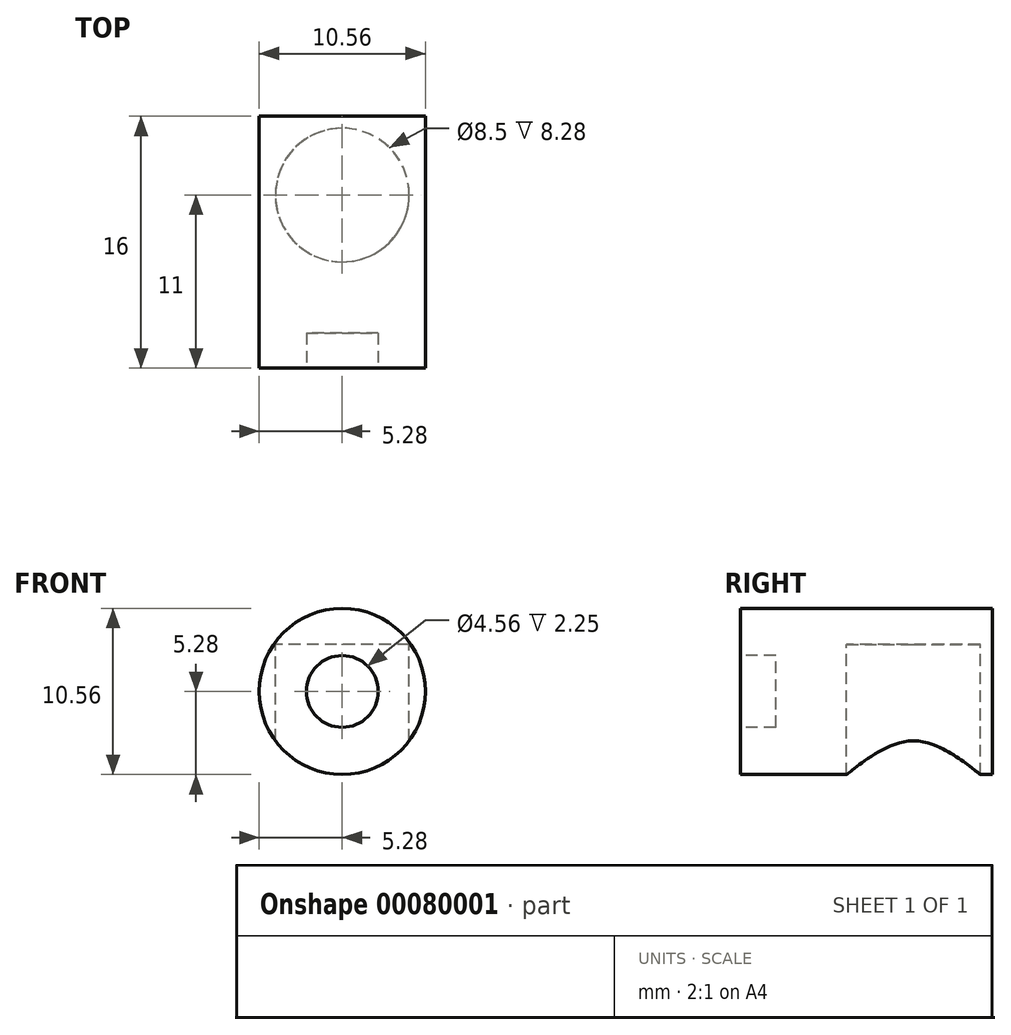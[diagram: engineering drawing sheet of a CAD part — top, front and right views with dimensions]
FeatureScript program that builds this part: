
annotation { "Feature Type Name" : "Feature", "Feature Type Description" : "" }
export const myFeature = defineFeature(function(context is Context, id is Id, definition is map)
    precondition{}
    {
        {
            var Q0;
            Q0=qCreatedBy(makeId("Front.planeOp"),FACE);
            var sketch = newSketch(context, id + "F0", { "sketchPlane" : qUnion([Q0])});
            skCircle(sketch, "E0", {"center": v(0, 0) * mm, "radius": 5.28 * mm});
            skSolve(sketch);
        }
        {
            var Q0;
            Q0 = qSketchRegion(id + "F0", true);
            extrude(context, id + "F1", {"entities" : qUnion([Q0]), "depth" : 16 * mm});
        }
        {
            var Q0;
            Q0=makeQuery(id+"F1.opExtrude","CAP_FACE",FACE,{"disambiguationData":[OSD([sQuery(id+"F0.wireOp",EDGE,"E0")])],"isStart":false});
            var sketch = newSketch(context, id + "F2", { "sketchPlane" : qUnion([Q0])});
            skCircle(sketch, "E1", {"center": v(0, 0) * mm, "radius": 2.28 * mm});
            skSolve(sketch);
        }
        {
            var Q0;
            Q0 = qSketchRegion(id + "F2", true);
            extrude(context, id + "F3", {"entities" : qUnion([Q0]), "operationType" : NewBodyOperationType.REMOVE, "oppositeDirection" : true, "depth" : 2.25 * mm});
        }
        {
            var Q0;
            Q0=qCreatedBy(makeId("Top.planeOp"),FACE);
            var sketch = newSketch(context, id + "F4", { "sketchPlane" : qUnion([Q0])});
            skCircle(sketch, "E2", {"center": v(0, -5) * mm, "radius": 4.25 * mm});
            skSolve(sketch);
        }
        {
            var Q0;
            Q0 = qSketchRegion(id + "F4", true);
            extrude(context, id + "F5", {"entities" : qUnion([Q0]), "operationType" : NewBodyOperationType.REMOVE, "oppositeDirection" : true, "depth" : 25 * mm, "hasSecondDirection" : true, "secondDirectionOppositeDirection" : false, "secondDirectionDepth" : 3 * mm});
        }
    });
